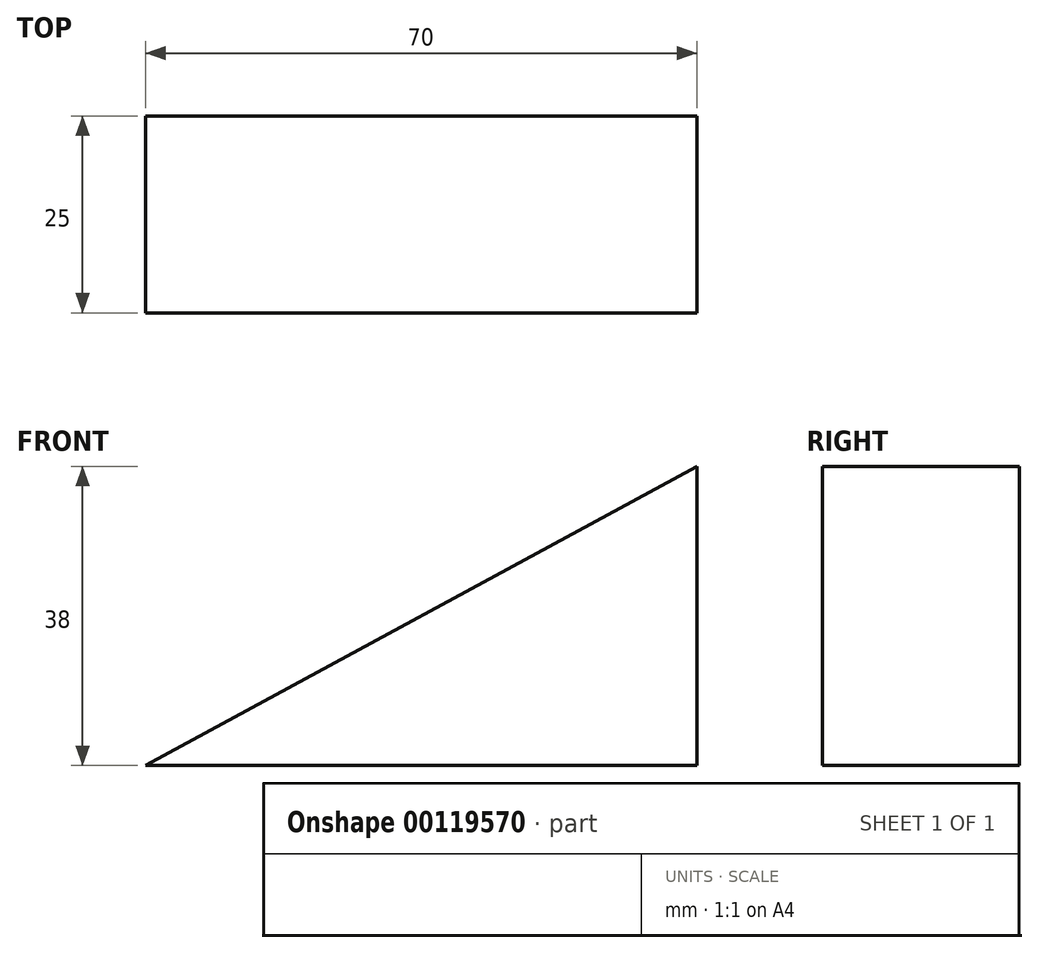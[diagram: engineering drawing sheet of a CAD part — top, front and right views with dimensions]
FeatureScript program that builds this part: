
annotation { "Feature Type Name" : "Feature", "Feature Type Description" : "" }
export const myFeature = defineFeature(function(context is Context, id is Id, definition is map)
    precondition{}
    {
        {
            var Q0;
            Q0=qCreatedBy(makeId("Front.planeOp"),FACE);
            var sketch = newSketch(context, id + "F0", { "sketchPlane" : qUnion([Q0])});
            skLineSegment(sketch, "E0", {"start": v(-29.76, 0) * mm, "end": v(40.24, 0) * mm});
            skLineSegment(sketch, "E1", {"start": v(40.24, 0) * mm, "end": v(40.24, 38) * mm});
            skLineSegment(sketch, "E2", {"start": v(40.24, 38) * mm, "end": v(-29.76, 0) * mm});
            skSolve(sketch);
        }
        {
            var Q0;
            Q0=makeQuery(id+"F0.imprint","IMPRINT",FACE,{"disambiguationData":[TD([[makeQuery(id+"F0.imprint","IMPRINT",EDGE,{"derivedFrom":sQuery(id+"F0.wireOp",EDGE,"E0")}),1.0]])]});
            extrude(context, id + "F1", {"entities" : qUnion([Q0]), "depth" : 25 * mm});
        }
    });
